# Revit family: ACO Q-Brake Vortex - Round Type - For Circular Manholes
name_source: partatom
category: Generic Models
revit_build: Autodesk Revit 2013 (Build: 20120221_2030(x64)
units: mm (PartAtom-declared; Revit-internal decimal feet)

## types (1)
- ACO Q-Brake Vortex - Round Type - For Circular Manholes
    ACO Hydraulic Design Software = http://www.acodesign.co.uk
    ACO Q-Brake Vortex - Design Flow – Max Discharge @ Design Head = Client to populate
    ACO Q-Brake Vortex Part No = Contact ACO for further details
    ACO Q-Brake Vortex body width = Contact ACO for further details
    ACO Q-Brake Vortex body Ø = Contact ACO for further details
    ACO Q-Brake Vortex orifice Ø = Contact ACO for further details
    ACO Q-Brake Vortex outlet pipe Ø = Client to populate
    Assembly Code = D2040
    Centre = 0 mm  [stored 0 ft]
    Cost = 0 $
    Design Head – Invert of outlet pipe to top water level = Client to populate
    Fax = +44 (0)1462 815895
    Installation guidelines = http://www.aco.co.uk
    Maintenance guidelines = http://www.aco.co.uk
    Manufacturer = ACO Technologies plc - ACO Water Management Division
    Model = ACO Q-Brake Vortex
    Model Description = Stormwater Flow Control System
    Price = POA - contact ACO
    Product Code = Contact ACO for bespoke product code
    Product Page URL = http://www.aco.co.uk
    Product brochure = http://www.aco.co.uk
    Q-Brake Vortex Material = Stainless Steel Grade 304
    Q-Brake Vortex Recycled Material Content = Between 40% - 90%
    Q-Brake VortexRecyclable = Fully recyclable
    Q-Brake Vortexl Colour = Silver
    Revision = 1
    SerialNumber = 0 mm  [stored 0 ft]
    TagNumber = 0 mm  [stored 0 ft]
    Telephone = +44 (0)1462 816666
    Type Comments = ACO Q-Brake Vortex Flow Control - To Suit Round Manhole
    URL = www.aco.co.uk

note: [stored X ft] marks values corroborated as IEEE doubles in the binary element streams (Revit-internal decimal feet)

## geometry (parser evidence)
native form markers: Sweep x4
no freeform markers — native parametric forms only
